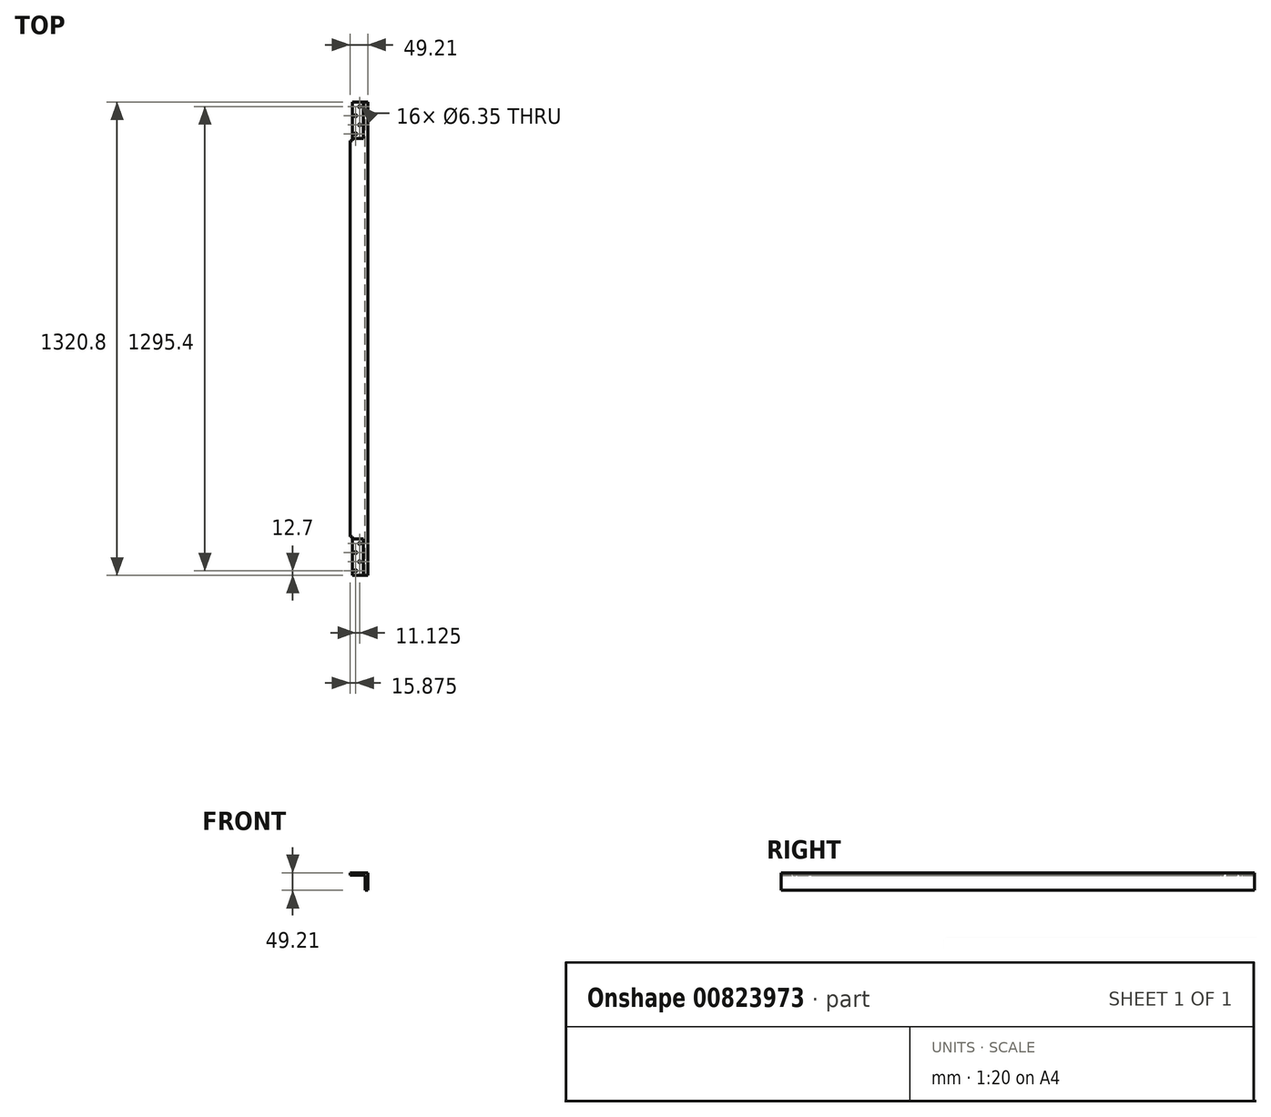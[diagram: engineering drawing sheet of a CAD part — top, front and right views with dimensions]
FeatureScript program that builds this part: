
annotation { "Feature Type Name" : "Feature", "Feature Type Description" : "" }
export const myFeature = defineFeature(function(context is Context, id is Id, definition is map)
    precondition{}
    {
        {
            var Q0;
            Q0=qCreatedBy(makeId("Front.planeOp"),FACE);
            var sketch = newSketch(context, id + "F0", { "sketchPlane" : qUnion([Q0])});
            skLineSegment(sketch, "E0.bottom", {"start": v(23.81, -23.81) * mm, "end": v(17.46, -23.81) * mm});
            skLineSegment(sketch, "E0.top", {"start": v(23.81, 25.4) * mm, "end": v(-25.4, 25.4) * mm});
            skLineSegment(sketch, "E0.left", {"start": v(23.81, -23.81) * mm, "end": v(23.81, 25.4) * mm});
            skPoint(sketch, "E0.middle", {"position": v(0, 0) * mm});
            skLineSegment(sketch, "E1", {"start": v(-25.4, 19.05) * mm, "end": v(17.46, 19.05) * mm});
            skLineSegment(sketch, "E2", {"start": v(17.46, 19.05) * mm, "end": v(17.46, -23.81) * mm});
            skLineSegment(sketch, "E3", {"start": v(-25.4, 25.4) * mm, "end": v(-25.4, 19.05) * mm});
            skSolve(sketch);
        }
        {
            var Q0;
            Q0=makeQuery(id+"F0.imprint","IMPRINT",FACE,{"disambiguationData":[TD([[makeQuery(id+"F0.imprint","IMPRINT",EDGE,{"derivedFrom":sQuery(id+"F0.wireOp",EDGE,"E0.bottom")}),-1.0]])]});
            extrude(context, id + "F1", {"entities" : qUnion([Q0]), "endBound" : BoundingType.SYMMETRIC, "depth" : 1320.8 * mm, "offsetDistance" : 25.4 * mm});
        }
        {
            var Q0;
            Q0=makeQuery(id+"F1.opExtrude","SWEPT_FACE",FACE,{"disambiguationData":[OSD([sQuery(id+"F0.wireOp",EDGE,"E0.top")])]});
            var sketch = newSketch(context, id + "F2", { "sketchPlane" : qUnion([Q0])});
            skLineSegment(sketch, "E4.left", {"start": v(-25.4, -552.55) * mm, "end": v(-25.4, -660.4) * mm});
            skLineSegment(sketch, "E4.right", {"start": v(11.13, -558.8) * mm, "end": v(11.13, -660.4) * mm});
            skLineSegment(sketch, "E5", {"start": v(11.13, -558.8) * mm, "end": v(-19.05, -558.8) * mm});
            skLineSegment(sketch, "E6", {"start": v(-19.05, -558.8) * mm, "end": v(-19.05, -660.4) * mm});
            skLineSegment(sketch, "E7", {"start": v(-19.05, -660.4) * mm, "end": v(11.13, -660.4) * mm});
            skCircle(sketch, "E8", {"center": v(1.6, -571.5) * mm, "radius": 3.18 * mm});
            skCircle(sketch, "E9", {"center": v(1.6, -622.3) * mm, "radius": 3.18 * mm});
            skCircle(sketch, "E10", {"center": v(-9.53, -596.9) * mm, "radius": 3.18 * mm});
            skCircle(sketch, "E11", {"center": v(-9.53, -647.7) * mm, "radius": 3.18 * mm});
            skLineSegment(sketch, "E12.top", {"start": v(-25.4, 552.55) * mm, "end": v(11.13, 552.55) * mm});
            skLineSegment(sketch, "E12.right", {"start": v(11.13, 660.4) * mm, "end": v(11.13, 552.55) * mm});
            skLineSegment(sketch, "E13", {"start": v(11.13, 660.4) * mm, "end": v(-19.05, 660.4) * mm});
            skLineSegment(sketch, "E14", {"start": v(-19.05, 660.4) * mm, "end": v(-19.05, 558.8) * mm});
            skLineSegment(sketch, "E15", {"start": v(-19.05, 558.8) * mm, "end": v(11.13, 558.8) * mm});
            skLineSegment(sketch, "E16", {"start": v(-19.05, 558.8) * mm, "end": v(-19.05, 552.55) * mm});
            skCircle(sketch, "E17", {"center": v(1.6, 647.7) * mm, "radius": 3.18 * mm});
            skCircle(sketch, "E18", {"center": v(1.6, 596.9) * mm, "radius": 3.18 * mm});
            skCircle(sketch, "E19", {"center": v(-9.52, 622.3) * mm, "radius": 3.18 * mm});
            skCircle(sketch, "E20", {"center": v(-9.52, 571.5) * mm, "radius": 3.18 * mm});
            skLineSegment(sketch, "E21", {"start": v(-19.05, -660.4) * mm, "end": v(-25.4, -660.4) * mm});
            skLineSegment(sketch, "E22", {"start": v(-25.4, -552.55) * mm, "end": v(11.13, -552.55) * mm});
            skLineSegment(sketch, "E23", {"start": v(11.13, -552.55) * mm, "end": v(11.13, -558.8) * mm});
            skLineSegment(sketch, "E24", {"start": v(-19.05, -558.8) * mm, "end": v(-19.05, -552.55) * mm});
            skLineSegment(sketch, "E25", {"start": v(-19.05, 660.4) * mm, "end": v(-25.4, 660.4) * mm});
            skLineSegment(sketch, "E26", {"start": v(-25.4, 660.4) * mm, "end": v(-25.4, 552.55) * mm});
            skSolve(sketch);
        }
        {
            var Q0;
            {var subQ1=sQuery(id+"F2.wireOp",EDGE,"E5");Q0=makeQuery(id+"F2.imprint","IMPRINT",FACE,{"disambiguationData":[TD([[makeQuery(id+"F2.imprint","IMPRINT",EDGE,{"derivedFrom":subQ1}),1.0]])]});}
            var Q1;
            {var subQ1=sQuery(id+"F2.wireOp",EDGE,"E13");Q1=makeQuery(id+"F2.imprint","IMPRINT",FACE,{"disambiguationData":[TD([[makeQuery(id+"F2.imprint","IMPRINT",EDGE,{"derivedFrom":subQ1}),1.0]])]});}
            extrude(context, id + "F3", {"entities" : qUnion([Q0, Q1]), "operationType" : NewBodyOperationType.REMOVE, "oppositeDirection" : true, "depth" : 3.17 * mm, "offsetDistance" : 25.4 * mm});
        }
        {
            var Q0;
            Q0=sQuery(id+"F2.wireOp",VERTEX,"E8.center");
            var Q1;
            Q1=sQuery(id+"F2.wireOp",VERTEX,"E10.center");
            var Q2;
            Q2=sQuery(id+"F2.wireOp",VERTEX,"E9.center");
            var Q3;
            Q3=sQuery(id+"F2.wireOp",VERTEX,"E11.center");
            var Q4;
            Q4=sQuery(id+"F2.wireOp",VERTEX,"E17.center");
            var Q5;
            Q5=sQuery(id+"F2.wireOp",VERTEX,"E19.center");
            var Q6;
            Q6=sQuery(id+"F2.wireOp",VERTEX,"E18.center");
            var Q7;
            Q7=sQuery(id+"F2.wireOp",VERTEX,"E20.center");
            var Q8;
            Q8=makeQuery(id+"F1.opExtrude","SWEPT_BODY",BODY,{"disambiguationData":[OSD([sQuery(id+"F0.wireOp",EDGE,"E0.bottom"),sQuery(id+"F0.wireOp",EDGE,"E0.top"),sQuery(id+"F0.wireOp",EDGE,"E0.left"),sQuery(id+"F0.wireOp",EDGE,"E1"),sQuery(id+"F0.wireOp",EDGE,"E2"),sQuery(id+"F0.wireOp",EDGE,"E3")])]});
            hole(context, id + "F4", {"style" : HoleStyle.SIMPLE, "endStyle" : HoleEndStyle.THROUGH, "holeDiameter" : 6.35 * mm, "majorDiameter" : 6.35 * mm, "isTappedThrough" : true, "tappedDepth" : 12.7 * mm, "tapClearance" : 3, "locations" : qUnion([Q0, Q1, Q2, Q3, Q4, Q5, Q6, Q7]), "scope" : qUnion([Q8])});
        }
        {
            var Q0;
            Q0=makeQuery(id+"F2.imprint","IMPRINT",FACE,{"disambiguationData":[TD([[makeQuery(id+"F2.imprint","IMPRINT",EDGE,{"derivedFrom":sQuery(id+"F2.wireOp",EDGE,"E14")}),-1.0]])]});
            var Q1;
            {var subQ1=sQuery(id+"F2.wireOp",EDGE,"E4.left");Q1=makeQuery(id+"F2.imprint","IMPRINT",FACE,{"disambiguationData":[TD([[makeQuery(id+"F2.imprint","IMPRINT",EDGE,{"derivedFrom":subQ1}),-1.0]])]});}
            extrude(context, id + "F5", {"entities" : qUnion([Q0, Q1]), "operationType" : NewBodyOperationType.REMOVE, "endBound" : BoundingType.THROUGH_ALL, "oppositeDirection" : true, "depth" : 25.4 * mm, "offsetDistance" : 25.4 * mm});
        }
    });
